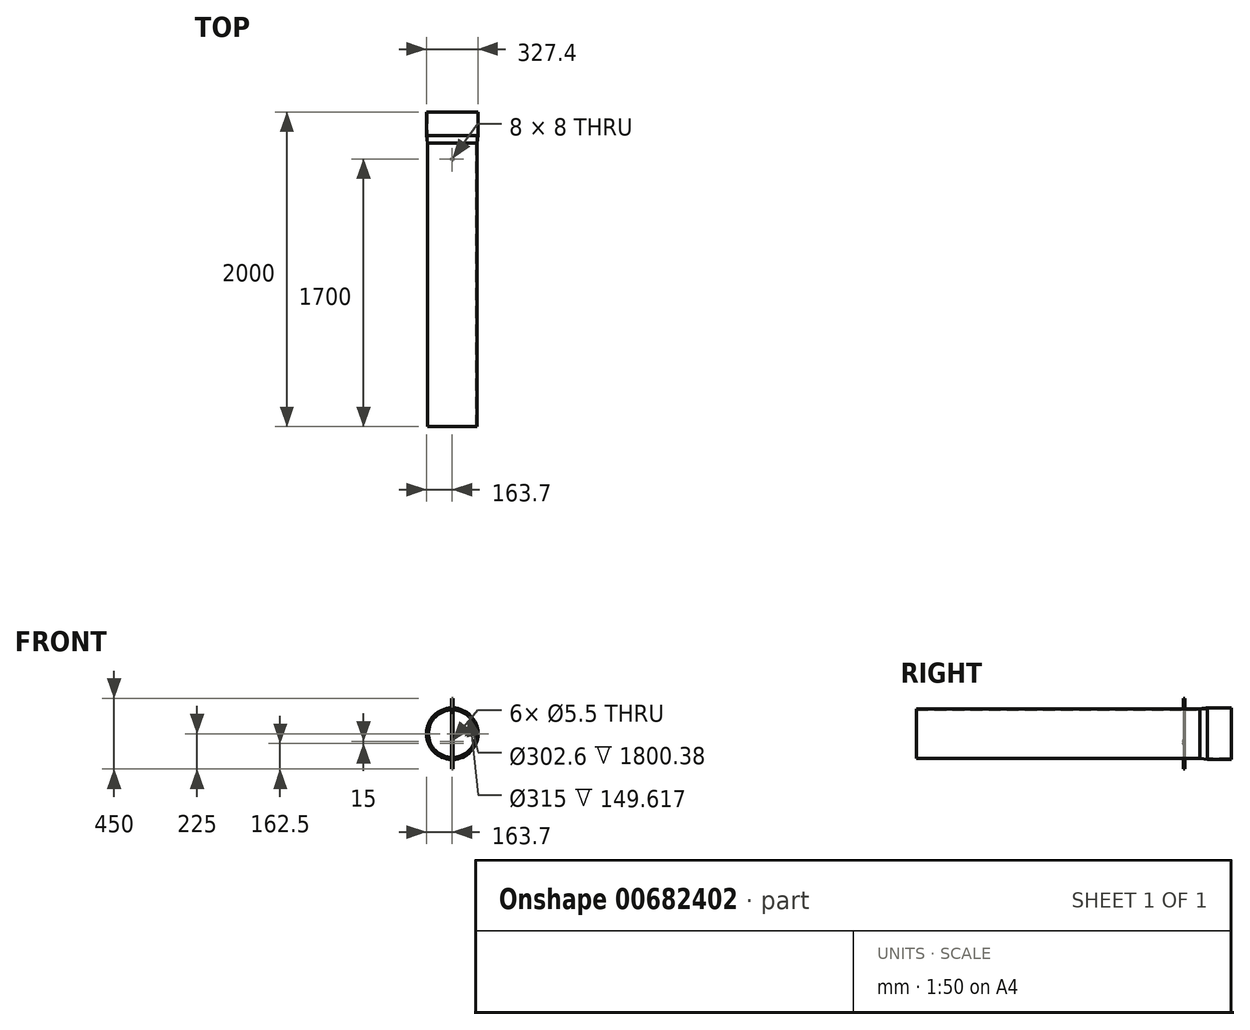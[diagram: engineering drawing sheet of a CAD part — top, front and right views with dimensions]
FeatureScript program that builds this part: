
annotation { "Feature Type Name" : "Feature", "Feature Type Description" : "" }
export const myFeature = defineFeature(function(context is Context, id is Id, definition is map)
    precondition{}
    {
        {
            var Q0;
            Q0=qCreatedBy(makeId("Front.planeOp"),FACE);
            var sketch = newSketch(context, id + "F0", { "sketchPlane" : qUnion([Q0])});
            skCircle(sketch, "E0", {"center": v(0, 0) * mm, "radius": 157.5 * mm});
            skSolve(sketch);
        }
        {
            var Q0;
            Q0=makeQuery(id+"F0.imprint","IMPRINT",FACE,{"disambiguationData":[TD([[makeQuery(id+"F0.imprint","IMPRINT",EDGE,{"derivedFrom":sQuery(id+"F0.wireOp",EDGE,"OQyqvsRQ-bjxP-x85P-igHw-BdMtP8STOQ0Q")}),-1.0]])]});
            var Q1;
            Q1=makeQuery(id+"F0.imprint","IMPRINT",FACE,{"disambiguationData":[TD([[makeQuery(id+"F0.imprint","IMPRINT",EDGE,{"derivedFrom":sQuery(id+"F0.wireOp",EDGE,"E0")}),1.0]])]});
            extrude(context, id + "F1", {"entities" : qUnion([Q0, Q1]), "depth" : 1800 * mm, "offsetDistance" : 25 * mm});
        }
        {
            var Q0;
            Q0=makeQuery(id+"F1.opExtrude","CAP_FACE",FACE,{"disambiguationData":[OSD([sQuery(id+"F0.wireOp",EDGE,"OQyqvsRQ-bjxP-x85P-igHw-BdMtP8STOQ0Q"),sQuery(id+"F0.wireOp",EDGE,"E0")])],"isStart":true});
            cPlane(context, id + "F2", {"entities" : qUnion([Q0]), "cplaneType" : CPlaneType.OFFSET, "offset" : 50 * mm, "width" : 150 * mm, "height" : 150 * mm});
        }
        {
            var Q0;
            Q0=qCreatedBy(id+"F2.planeOp",FACE);
            var sketch = newSketch(context, id + "F3", { "sketchPlane" : qUnion([Q0])});
            skCircle(sketch, "E1", {"center": v(0, 0) * mm, "radius": 163.7 * mm});
            skSolve(sketch);
        }
        {
            var Q1;
            Q1=makeQuery(id+"F3.imprint","IMPRINT",FACE,{"disambiguationData":[TD([[makeQuery(id+"F3.imprint","IMPRINT",EDGE,{"derivedFrom":sQuery(id+"F3.wireOp",EDGE,"E1")}),1.0]])]});
            var Q2;
            Q2=makeQuery(id+"F1.opExtrude","CAP_FACE",FACE,{"disambiguationData":[OSD([sQuery(id+"F0.wireOp",EDGE,"E0")])],"isStart":true});
            loft(context, id + "F4", {"operationType" : NewBodyOperationType.ADD, "sheetProfilesArray" : [{ "sheetProfileEntities" : qUnion([Q1]) }, { "sheetProfileEntities" : qUnion([Q2]) }]});
        }
        {
            var Q0;
            Q0=makeQuery(id+"F4.opLoft","CAP_FACE",FACE,{"disambiguationData":[OSD([makeQuery(id+"F3.imprint","IMPRINT",FACE,{"disambiguationData":[TD([[makeQuery(id+"F3.imprint","IMPRINT",EDGE,{"derivedFrom":sQuery(id+"F3.wireOp",EDGE,"E1")}),1.0]])]})])],"isStart":true});
            extrude(context, id + "F5", {"entities" : qUnion([Q0]), "operationType" : NewBodyOperationType.ADD, "depth" : 150 * mm, "offsetDistance" : 25 * mm});
        }
        {
            var Q0;
            Q0=makeQuery(id+"F5.opExtrude","CAP_FACE",FACE,{"disambiguationData":[OSD([makeQuery(id+"F3.imprint","IMPRINT",FACE,{"disambiguationData":[TD([[makeQuery(id+"F3.imprint","IMPRINT",EDGE,{"derivedFrom":sQuery(id+"F3.wireOp",EDGE,"E1")}),1.0]])]})])],"isStart":false});
            var Q1;
            Q1=makeQuery(id+"F1.opExtrude","CAP_FACE",FACE,{"disambiguationData":[OSD([sQuery(id+"F0.wireOp",EDGE,"E0")])],"isStart":false});
            shell(context, id + "F6", {"entities" : qUnion([Q0, Q1]), "thickness" : 6.2 * mm});
        }
        {
            var Q0;
            Q0=qCreatedBy(makeId("Top.planeOp"),FACE);
            var sketch = newSketch(context, id + "F7", { "sketchPlane" : qUnion([Q0])});
            skLineSegment(sketch, "E2.bottom", {"start": v(5, -105) * mm, "end": v(-5, -105) * mm});
            skLineSegment(sketch, "E2.top", {"start": v(5, -95) * mm, "end": v(-5, -95) * mm});
            skLineSegment(sketch, "E2.left", {"start": v(5, -105) * mm, "end": v(5, -95) * mm});
            skLineSegment(sketch, "E2.right", {"start": v(-5, -105) * mm, "end": v(-5, -95) * mm});
            skPoint(sketch, "E2.middle", {"position": v(0, -100) * mm});
            skLineSegment(sketch, "E3", {"start": v(0, 49.42) * mm, "end": v(0, -144.99) * mm, "construction": true});
            skSolve(sketch);
        }
        {
            var Q0;
            Q0=makeQuery(id+"F7.imprint","IMPRINT",FACE,{"disambiguationData":[TD([[makeQuery(id+"F7.imprint","IMPRINT",EDGE,{"derivedFrom":sQuery(id+"F7.wireOp",EDGE,"E2.bottom")}),-1.0]])]});
            extrude(context, id + "F8", {"entities" : qUnion([Q0]), "operationType" : NewBodyOperationType.REMOVE, "endBound" : BoundingType.SYMMETRIC, "oppositeDirection" : true, "depth" : 700 * mm, "offsetDistance" : 25 * mm});
        }
        {
            var Q0;
            Q0 = qSketchRegion(id + "F7", true);
            extrude(context, id + "F9", {"entities" : qUnion([Q0]), "endBound" : BoundingType.SYMMETRIC, "depth" : 450 * mm, "offsetDistance" : 25 * mm});
        }
        {
            var Q0;
            Q0=makeQuery(id+"F9.opExtrude","CAP_FACE",FACE,{"disambiguationData":[OSD([sQuery(id+"F7.wireOp",EDGE,"E2.bottom"),sQuery(id+"F7.wireOp",EDGE,"E2.top"),sQuery(id+"F7.wireOp",EDGE,"E2.left"),sQuery(id+"F7.wireOp",EDGE,"E2.right")])],"isStart":false});
            var Q1;
            Q1=makeQuery(id+"F9.opExtrude","CAP_FACE",FACE,{"disambiguationData":[OSD([sQuery(id+"F7.wireOp",EDGE,"E2.bottom"),sQuery(id+"F7.wireOp",EDGE,"E2.top"),sQuery(id+"F7.wireOp",EDGE,"E2.left"),sQuery(id+"F7.wireOp",EDGE,"E2.right")])],"isStart":true});
            shell(context, id + "F10", {"entities" : qUnion([Q0, Q1]), "thickness" : 1 * mm});
        }
        {
            var Q0;
            Q0=makeQuery(id+"F9.opExtrude","SWEPT_FACE",FACE,{"disambiguationData":[OSD([sQuery(id+"F7.wireOp",EDGE,"E2.bottom")])]});
            var sketch = newSketch(context, id + "F11", { "sketchPlane" : qUnion([Q0])});
            skLineSegment(sketch, "E4", {"start": v(0, 12.03) * mm, "end": v(0, -86.8) * mm, "construction": true});
            skPoint(sketch, "E5", {"position": v(0, -47.5) * mm});
            skPoint(sketch, "E6", {"position": v(0, -62.5) * mm});
            skLineSegment(sketch, "E7.bottom", {"start": v(-5, -37.5) * mm, "end": v(5, -37.5) * mm});
            skLineSegment(sketch, "E7.top", {"start": v(-5, -72.5) * mm, "end": v(5, -72.5) * mm});
            skLineSegment(sketch, "E7.left", {"start": v(-5, -37.5) * mm, "end": v(-5, -72.5) * mm});
            skLineSegment(sketch, "E7.right", {"start": v(5, -37.5) * mm, "end": v(5, -72.5) * mm});
            skSolve(sketch);
        }
        {
            var Q0;
            Q0=makeQuery(id+"F11.imprint","IMPRINT",FACE,{"disambiguationData":[TD([[makeQuery(id+"F11.imprint","IMPRINT",EDGE,{"derivedFrom":sQuery(id+"F11.wireOp",EDGE,"E7.bottom")}),-1.0]])]});
            extrude(context, id + "F12", {"entities" : qUnion([Q0]), "depth" : 2 * mm, "offsetDistance" : 25 * mm});
        }
        {
            var Q0;
            Q0=sQuery(id+"F11.wireOp",VERTEX,"E5");
            var Q1;
            Q1=sQuery(id+"F11.wireOp",VERTEX,"E6");
            var Q2;
            Q2=makeQuery(id+"F9.opExtrude","SWEPT_BODY",BODY,{"disambiguationData":[OSD([sQuery(id+"F7.wireOp",EDGE,"E2.bottom"),sQuery(id+"F7.wireOp",EDGE,"E2.top"),sQuery(id+"F7.wireOp",EDGE,"E2.left"),sQuery(id+"F7.wireOp",EDGE,"E2.right")])]});
            hole(context, id + "F13", {"style" : HoleStyle.SIMPLE, "endStyle" : HoleEndStyle.THROUGH, "standardTappedOrClearance" : lookupTablePath({ "standard" : "ISO", "fit" : "Normal", "size" : "M5", "type" : "Clearance" }), "standardBlindInLast" : lookupTablePath({ "fit" : "Standard", "standard" : "ISO", "size" : "M5", "type" : "Clearance" }), "holeDiameter" : 5.5 * mm, "majorDiameter" : 5 * mm, "isTappedThrough" : true, "tappedDepth" : 17.6 * mm, "tapClearance" : 3, "locations" : qUnion([Q0, Q1]), "scope" : qUnion([Q2])});
        }
        {
            var Q0;
            Q0=sQuery(id+"F11.wireOp",VERTEX,"E5");
            var Q1;
            Q1=sQuery(id+"F11.wireOp",VERTEX,"E6");
            var Q2;
            Q2=makeQuery(id+"F12.opExtrude","SWEPT_BODY",BODY,{"disambiguationData":[OSD([sQuery(id+"F11.wireOp",EDGE,"E7.bottom"),sQuery(id+"F11.wireOp",EDGE,"E7.top"),sQuery(id+"F11.wireOp",EDGE,"E7.left"),sQuery(id+"F11.wireOp",EDGE,"E7.right")])]});
            hole(context, id + "F14", {"style" : HoleStyle.SIMPLE, "endStyle" : HoleEndStyle.THROUGH, "oppositeDirection" : true, "standardTappedOrClearance" : lookupTablePath({ "standard" : "ISO", "fit" : "Normal", "size" : "M5", "type" : "Clearance" }), "standardBlindInLast" : lookupTablePath({ "fit" : "Standard", "standard" : "ISO", "size" : "M5", "type" : "Clearance" }), "holeDiameter" : 5.5 * mm, "majorDiameter" : 5 * mm, "isTappedThrough" : true, "tappedDepth" : 17.6 * mm, "tapClearance" : 3, "locations" : qUnion([Q0, Q1]), "scope" : qUnion([Q2])});
        }
    });
